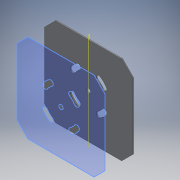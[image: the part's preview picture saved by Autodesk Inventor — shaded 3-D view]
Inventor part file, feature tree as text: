
AUTODESK INVENTOR PART (.ipt)
format: ipt  version: 2017 (Build 210142000, 142)  size: 142,336 bytes
history: native  units: mm
features: extrude x1, other x1, chamfer x1, plane x1, sketch x1
ambient origin geometry x8: Origin, YZ Plane, XZ Plane, XY Plane, X Axis, Y Axis, Z Axis, Center Point
bodies: Solid1 (feature_tree)
feature tree (5):
  extrude  "Extrusion1"  Depth=304.8mm
  other  "Work Axis1"
  chamfer  "Chamfer1"  Distance=3.175mm
  plane  "Work Plane1"
  sketch  "Sketch1"  dims[d1=304.8mm d2=304.8mm d3=3.175mm d4=0.0mm d5=35.0mm d6=38.1mm d7=2.0mm d8=45.0deg d9=40.0mm d11=360.0deg d13=18.0mm d14=15.0mm]
